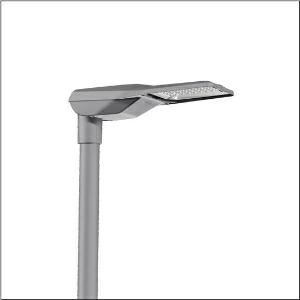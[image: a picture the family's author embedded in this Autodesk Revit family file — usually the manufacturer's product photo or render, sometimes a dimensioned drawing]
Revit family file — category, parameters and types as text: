
# Revit family: streetlight_sl_21_iq_mini___stw1_0a_5xe2e31d08hb_6dd6
name_source: partatom
category: Lighting Fixtures
units: mm (PartAtom-declared; Revit-internal decimal feet)

## family parameters
Cut with Voids When Loaded = No
Host = Face
Light Source = No
Part Type = Normal
Room Calculation Point = No
Round Connector Dimension = Use Diameter
Shared = No

## types (1)
- --- (1 x LED, 9450 lm, 70.9 W, 3000K)
    Apparent Load = 71 VA
    CIE Flux Codes = 38 75 98 100 100
    Color Rendering = 70
    Color Temperature = 3000K
    Default Elevation = 1800 mm
    Description = Streetlight SL 21 iQ mini, mast luminaire, primary light control with lens, of PMMA, primary optical cover: cover, of toughened safety glass, transparent, light distribution: STW1.0a, light emission: direct distribution, primary light characteristic: asymmetric, installation type: post-top, side-entry, LED, High Power LED, rated luminous flux: 9.450lm, luminous efficacy: 133lm/W, light colour: 730, colour temperature: 3000K, control: Auto-Match, Temp-Guard, Lumen-Switch, Night-Set, Smart-Wire, Light-Fading, Desk-Remote (wireless, voltage-free reading and setting of iQ features in the workshop via application-optimized NFC function/RFID function), optimised constant luminous flux control (CLO 2.0), presetting dimming linear, mains connection: 220..240V, AC, 50/60Hz, start of lifetime: 71W, end of service life: 75W, reduction: 31W, luminaire housing, of diecast aluminium, powder-coated, Siteco® metallic grey (DB 702S), corrosivity category C5 mid according to DIN EN ISO 12944, please order mast flange separately, inclination adjustable: 0°, 5°, 10°, 15°, sealing non-destructively replaceable, multi-level sealing system, length: 628mm, width: 235mm, height: 110mm, mast flange for spigot size: 42mm (side-entry): 5XC10008XM4, 60/48mm (side-entry/post-top): 5XC10108XM2, 76/60mm (side-entry/post-top): 5XC10108XM1, protection rating (complete): IP66, insulation class (complete): insulation class II (safety insulation), certification: CE, ENEC, ENEC+, VDE, impact resistance: IK09, permissible operating ambient temperature for outdoor applications: -40..+50°C, standard-compliant lighting for roads and squares, packaging unit: 1 piece

Light Distribution: STW1.0a
    Height = 110 mm
    Lamp = 1 x LED
    Lamp Light Flux = 9450 lm
    Lamp Power = 70.9 W
    Lamp count = 1
    Length = 625 mm
    Luminous efficacy = 133 lm/W
    Manufacturer = Siteco
    ModVariant = No
    Model = 5XE2E31D08HB
    Number of Poles = 1
    OnlyDefault = Yes
    Power Factor = 1
    Product Name = Streetlight SL 21 iQ mini | STW1.0a
    Product group = mast luminaire | pylon top
    ProductGroupID = 6100
    Protection Class = Protection class II
    Protection Degree = IP 66
    RLX_Detail_Level = 1
    RLX_Emergency_Light_Flux = 0 lm
    RLX_Emergency_Type = 0
    RLX_Emergency_Type_DB = No
    RlxData = <blob elided: 93513 chars, md5=3c52e833>
    Socket = socket
    Standby Power = 0 W
    System Light Flux = 9450 lm
    System Power = 71 W
    Type Comments = factory setting: luminous flux: 100 % | dim-lin: 254 | 711 mA
    Type Image = l_1003519.jpg
    URL = http://relux.com
    VarID = @adj_090191
    Voltage = 0 V
    Weight = 0.00 kg
    Width = 234 mm

## geometry (parser evidence)
native form markers: Blend x4, Sweep x11
no freeform markers — native parametric forms only
